# Revit family: PRD_AR_SoapDpnsrs_RODANSoapDispenser_RODX619
name_source: partatom
category: Specialty Equipment
revit_build: Autodesk Revit 2018 (Build: 20190510_1515(x64)
units: mm (PartAtom-declared; Revit-internal decimal feet)

## family parameters
Cut with Voids When Loaded = No
Host = Face
OmniClass Number = 23.40.20.21.34
OmniClass Title = Soap Holders, Dispensers
Part Type = Normal
Room Calculation Point = No
Round Connector Dimension = Use Diameter
Shared = No

## types (1)
- RODX619
    AssetType = Fixed
    BIMObjectName = PRD_AR_SoapDispensers_RODANSoapDispenser_RODX619
    Category = Pr_40_70_22_81, Soap dispensers
    Color = Stainless steel
    Default Elevation = 1050 mm
    Description = Soap dispenser for wall mounting, stainless steel, surface satin finished, material thickness 0.8 mm, folded front cover, cylinder lock with KWC standard key, suitable for liquid soaps and lotions, 1 liter soap tank, push button on front, incl. stainless steel screws and dowels.
    DurationUnit = year
    Features = stainless steel, 0.80 mm, satin finished, wall mounting, 200x140x132 mm (WxHxD)
    FillingVolume = 1.00 L
    Finish = Satin finished
    Form = Wall mounted
    GrossWeight = 1.24 kg
    IfcExportAs = IfcFurnitureType
    IfcExportType = NOTDEFINED
    IntegralAccessories = Stainless steel screws and dowels incl.
    Lock = key-lock
    MainColor = Stainless steel
    Manufacturer = KWC Group AG
    ManufacturerName = KWC Group AG
    ManufacturerURL = www.kwc.com
    Material = Stainless steel
    MaterialsBody = Stainless steel
    MaterialsFinishAndColour = Stainless steel, satin finished
    Model = RODX619
    ModelNumber = 2000090068
    ModelReference = RODX619
    NBSDescription = Soap dispensers
    NBSReference = 45-35-72/358
    Name = RODAN Soap dispenser RODX619
    NetWeight = 1.12 kg
    NominalDepth = 132 mm  [stored 0.433071 ft]
    NominalHeight = 140 mm  [stored 0.459318 ft]
    NominalLength = 200 mm  [stored 0.656168 ft]
    NominalWidth = 200 mm  [stored 0.656168 ft]
    Operation = Manual
    ProductInformation = https://pim.kwc.com
    Size = 200x140x132 mm
    SoapDispenserMaterial = PRD_AR_StainlessSteel_SatinFinished
    Style = Soap dispenser
    TypeOfConsumable = Liquid soap
    TypeOfSoapContainer = Integrated refillable bag
    URL = www.kwc.com
    Uniclass2015Code = Pr_40_70_22_81
    Uniclass2015Title = Soap dispensers
    Uniclass2015Version = Products v1.7
    Version = 1
    WarrantyDurationUnit = year

note: [stored X ft] marks values corroborated as IEEE doubles in the binary element streams (Revit-internal decimal feet)

## geometry (parser evidence)
native form markers: Sweep x2
no freeform markers — native parametric forms only
